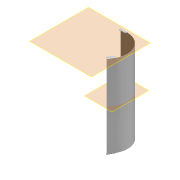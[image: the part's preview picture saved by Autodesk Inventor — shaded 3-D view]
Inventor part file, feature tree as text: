
AUTODESK INVENTOR PART (.ipt)
format: ipt  version: 2014 (Build 180170000, 170)  size: 203,776 bytes
history: native  units: mm
features: sketch x5, extrude x5, plane x3, fillet x3, reference x3, mirror x1, projected_geometry x1
ambient origin geometry x8: Origin, YZ Plane, XZ Plane, XY Plane, X Axis, Y Axis, Z Axis, Center Point
bodies: Solid1 (feature_tree)
feature tree (21):
  plane  "Work Plane1"
  sketch  "Sketch1"  dims[d0=1.5mm d1=551.0mm d2=0.0mm]
  plane  "Work Plane2"
  extrude  "Extrusion1"  Depth=551.0mm TaperAngle=0.0deg
  extrude  "Extrusion2"  Depth=15.0mm
  fillet  "Fillet4"  Radius=1.5mm
  extrude  "Extrusion5"  Depth=6.0mm
  fillet  "Fillet5"  Radius=4.0mm
  plane  "Work Plane5"
  mirror  "Mirror3"
  extrude  "Extrusion7"  Depth=4.0mm
  extrude  "Extrusion8"  Depth=1.5mm
  fillet  "Fillet7"  Radius=2.0mm
  reference  "Reference1"
  reference  "Reference2"
  reference  "Reference3"
  sketch  "Sketch2"  dims[d3=15.0mm d4=15.0mm d5=1.5mm d6=0.0mm]
  sketch  "Sketch5"  dims[d16=6.0mm d17=4.0mm d18=4.0mm]
  projected_geometry  "Projected Loop1"
  sketch  "Sketch7"  dims[d19=4.0mm d20=4.0mm]
  sketch  "Sketch8"  dims[d21=2.0mm d22=0.0mm d25=1.5mm d27=2.0mm d28=0.0mm d29=2.0mm d30=0.0mm d31=3.0mm]
